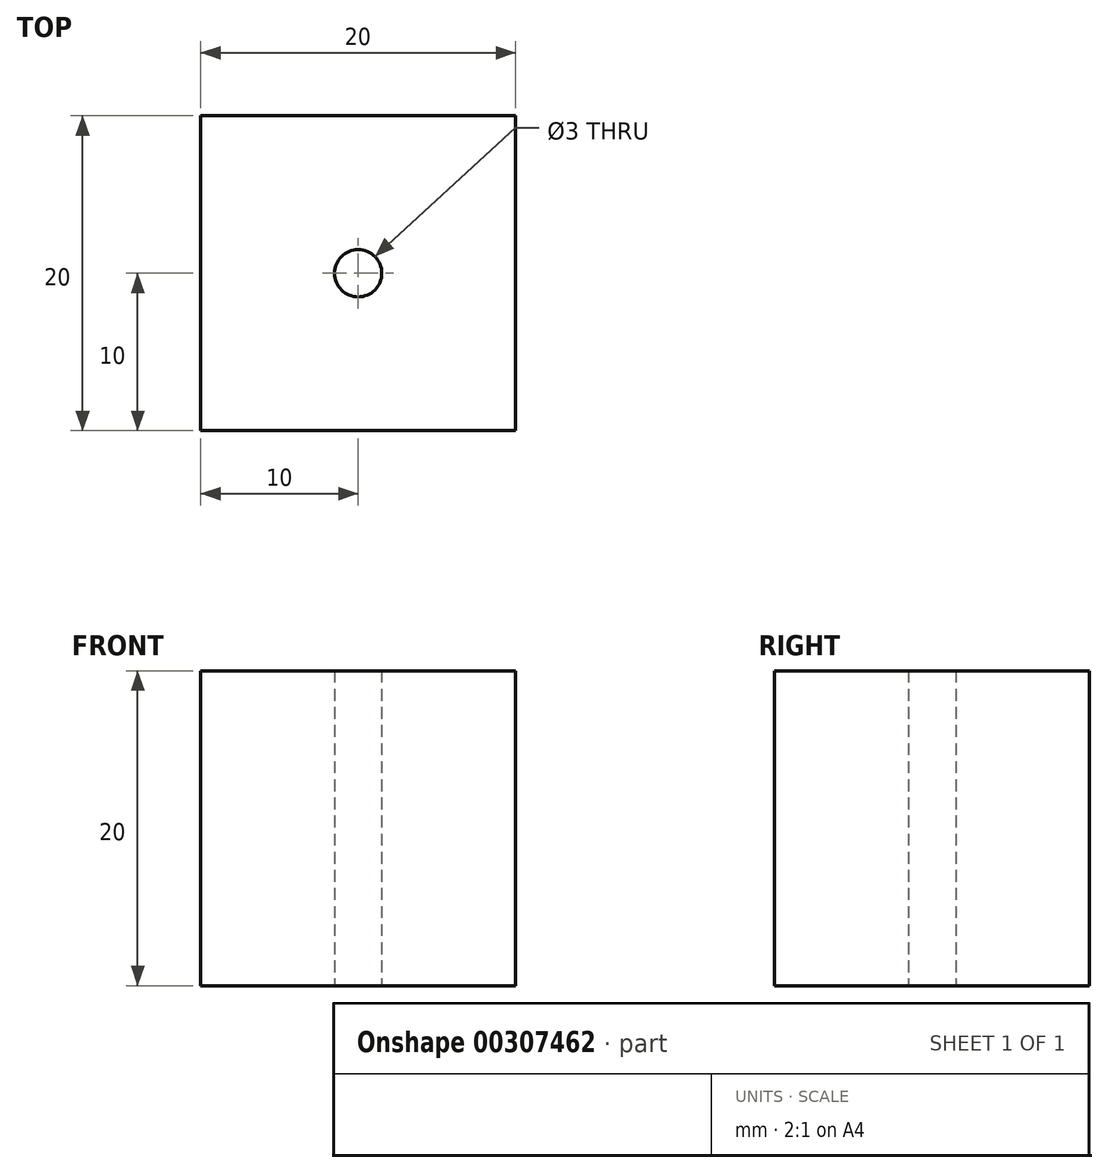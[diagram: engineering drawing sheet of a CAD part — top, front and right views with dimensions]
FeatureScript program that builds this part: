
annotation { "Feature Type Name" : "Feature", "Feature Type Description" : "" }
export const myFeature = defineFeature(function(context is Context, id is Id, definition is map)
    precondition{}
    {
        {
            var Q0;
            Q0=qCreatedBy(makeId("Top.planeOp"),FACE);
            var sketch = newSketch(context, id + "F0", { "sketchPlane" : qUnion([Q0])});
            skLineSegment(sketch, "E0.bottom", {"start": v(0, 0) * mm, "end": v(20, 0) * mm});
            skLineSegment(sketch, "E0.top", {"start": v(0, 20) * mm, "end": v(20, 20) * mm});
            skLineSegment(sketch, "E0.left", {"start": v(0, 0) * mm, "end": v(0, 20) * mm});
            skLineSegment(sketch, "E0.right", {"start": v(20, 0) * mm, "end": v(20, 20) * mm});
            skLineSegment(sketch, "E1", {"start": v(10, 20) * mm, "end": v(10, 0) * mm});
            skLineSegment(sketch, "E2", {"start": v(0, 10) * mm, "end": v(20, 10) * mm});
            skLineSegment(sketch, "E3", {"start": v(10, 20) * mm, "end": v(10, 0) * mm, "construction": true});
            skLineSegment(sketch, "E4", {"start": v(0, 10) * mm, "end": v(20, 10) * mm, "construction": true});
            skCircle(sketch, "E5", {"center": v(10, 10) * mm, "radius": 1.5 * mm});
            skSolve(sketch);
        }
        {
            var Q0;
            Q0 = qSketchRegion(id + "F0", true);
            extrude(context, id + "F1", {"entities" : qUnion([Q0]), "depth" : 20 * mm});
        }
    });
